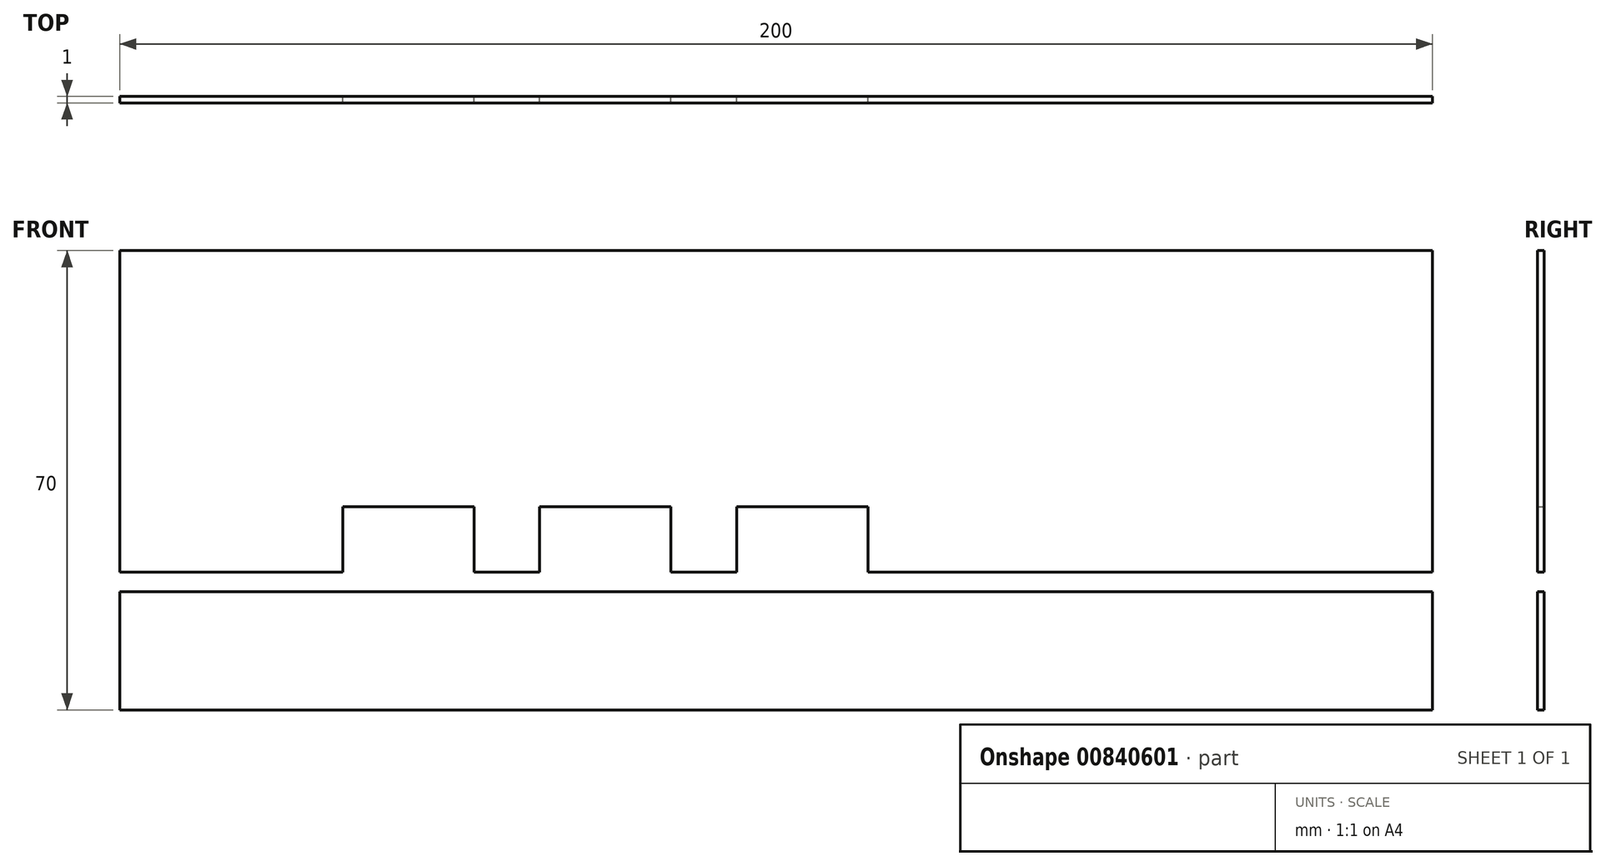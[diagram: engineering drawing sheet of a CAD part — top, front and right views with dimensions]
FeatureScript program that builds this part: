
annotation { "Feature Type Name" : "Feature", "Feature Type Description" : "" }
export const myFeature = defineFeature(function(context is Context, id is Id, definition is map)
    precondition{}
    {
        {
            var Q0;
            Q0=qCreatedBy(makeId("Front.planeOp"),FACE);
            var sketch = newSketch(context, id + "F0", { "sketchPlane" : qUnion([Q0])});
            skLineSegment(sketch, "E0.bottom", {"start": v(0, 18) * mm, "end": v(200, 18) * mm});
            skLineSegment(sketch, "E0.top", {"start": v(0, 21) * mm, "end": v(200, 21) * mm});
            skLineSegment(sketch, "E0.left", {"start": v(0, 18) * mm, "end": v(0, 21) * mm});
            skLineSegment(sketch, "E0.right", {"start": v(200, 18) * mm, "end": v(200, 21) * mm});
            skLineSegment(sketch, "E1.bottom", {"start": v(34, 21) * mm, "end": v(54, 21) * mm});
            skLineSegment(sketch, "E1.top", {"start": v(34, 31) * mm, "end": v(54, 31) * mm});
            skLineSegment(sketch, "E1.left", {"start": v(34, 21) * mm, "end": v(34, 31) * mm});
            skLineSegment(sketch, "E1.right", {"start": v(54, 21) * mm, "end": v(54, 31) * mm});
            skLineSegment(sketch, "E2.bottom", {"start": v(64, 21) * mm, "end": v(84, 21) * mm});
            skLineSegment(sketch, "E2.top", {"start": v(64, 31) * mm, "end": v(84, 31) * mm});
            skLineSegment(sketch, "E2.left", {"start": v(64, 21) * mm, "end": v(64, 31) * mm});
            skLineSegment(sketch, "E2.right", {"start": v(84, 21) * mm, "end": v(84, 31) * mm});
            skLineSegment(sketch, "E3.bottom", {"start": v(94, 21) * mm, "end": v(114, 21) * mm});
            skLineSegment(sketch, "E3.top", {"start": v(94, 31) * mm, "end": v(114, 31) * mm});
            skLineSegment(sketch, "E3.left", {"start": v(94, 21) * mm, "end": v(94, 31) * mm});
            skLineSegment(sketch, "E3.right", {"start": v(114, 21) * mm, "end": v(114, 31) * mm});
            skSolve(sketch);
        }
        {
            var Q0;
            Q0=qSketchRegion(id+"F0",true);
            extrude(context, id + "F1", {"entities" : qUnion([Q0]), "depth" : 1 * mm, "offsetDistance" : 25 * mm});
        }
        {
            var Q0;
            Q0=qCreatedBy(makeId("Front.planeOp"),FACE);
            var sketch = newSketch(context, id + "F2", { "sketchPlane" : qUnion([Q0])});
            skLineSegment(sketch, "E4.bottom", {"start": v(0, 0) * mm, "end": v(200, 0) * mm});
            skLineSegment(sketch, "E4.top", {"start": v(0, 70) * mm, "end": v(200, 70) * mm});
            skLineSegment(sketch, "E4.left", {"start": v(0, 0) * mm, "end": v(0, 70) * mm});
            skLineSegment(sketch, "E4.right", {"start": v(200, 0) * mm, "end": v(200, 70) * mm});
            skSolve(sketch);
        }
        {
            var Q0;
            Q0 = qSketchRegion(id + "F2", true);
            extrude(context, id + "F3", {"entities" : qUnion([Q0]), "depth" : 1 * mm, "offsetDistance" : 25 * mm});
        }
        {
            var Q0;
            Q0=makeQuery(id+"F1.opExtrude","SWEPT_BODY",BODY,{"disambiguationData":[OSD([sQuery(id+"F0.wireOp",EDGE,"E0.bottom"),sQuery(id+"F0.wireOp",EDGE,"E0.top"),sQuery(id+"F0.wireOp",EDGE,"E0.left"),sQuery(id+"F0.wireOp",EDGE,"E0.right"),sQuery(id+"F0.wireOp",EDGE,"E1.top"),sQuery(id+"F0.wireOp",EDGE,"E1.left"),sQuery(id+"F0.wireOp",EDGE,"E1.right"),sQuery(id+"F0.wireOp",EDGE,"E2.top"),sQuery(id+"F0.wireOp",EDGE,"E2.left"),sQuery(id+"F0.wireOp",EDGE,"E2.right"),sQuery(id+"F0.wireOp",EDGE,"E3.top"),sQuery(id+"F0.wireOp",EDGE,"E3.left"),sQuery(id+"F0.wireOp",EDGE,"E3.right")])]});
            var Q1;
            Q1=makeQuery(id+"F3.opExtrude","SWEPT_BODY",BODY,{"disambiguationData":[OSD([sQuery(id+"F2.wireOp",EDGE,"E4.bottom"),sQuery(id+"F2.wireOp",EDGE,"E4.top"),sQuery(id+"F2.wireOp",EDGE,"E4.left"),sQuery(id+"F2.wireOp",EDGE,"E4.right")])]});
            booleanBodies(context, id + "F4", {"operationType" : BooleanOperationType.SUBTRACTION, "tools" : qUnion([Q0]), "targets" : qUnion([Q1])});
        }
    });
